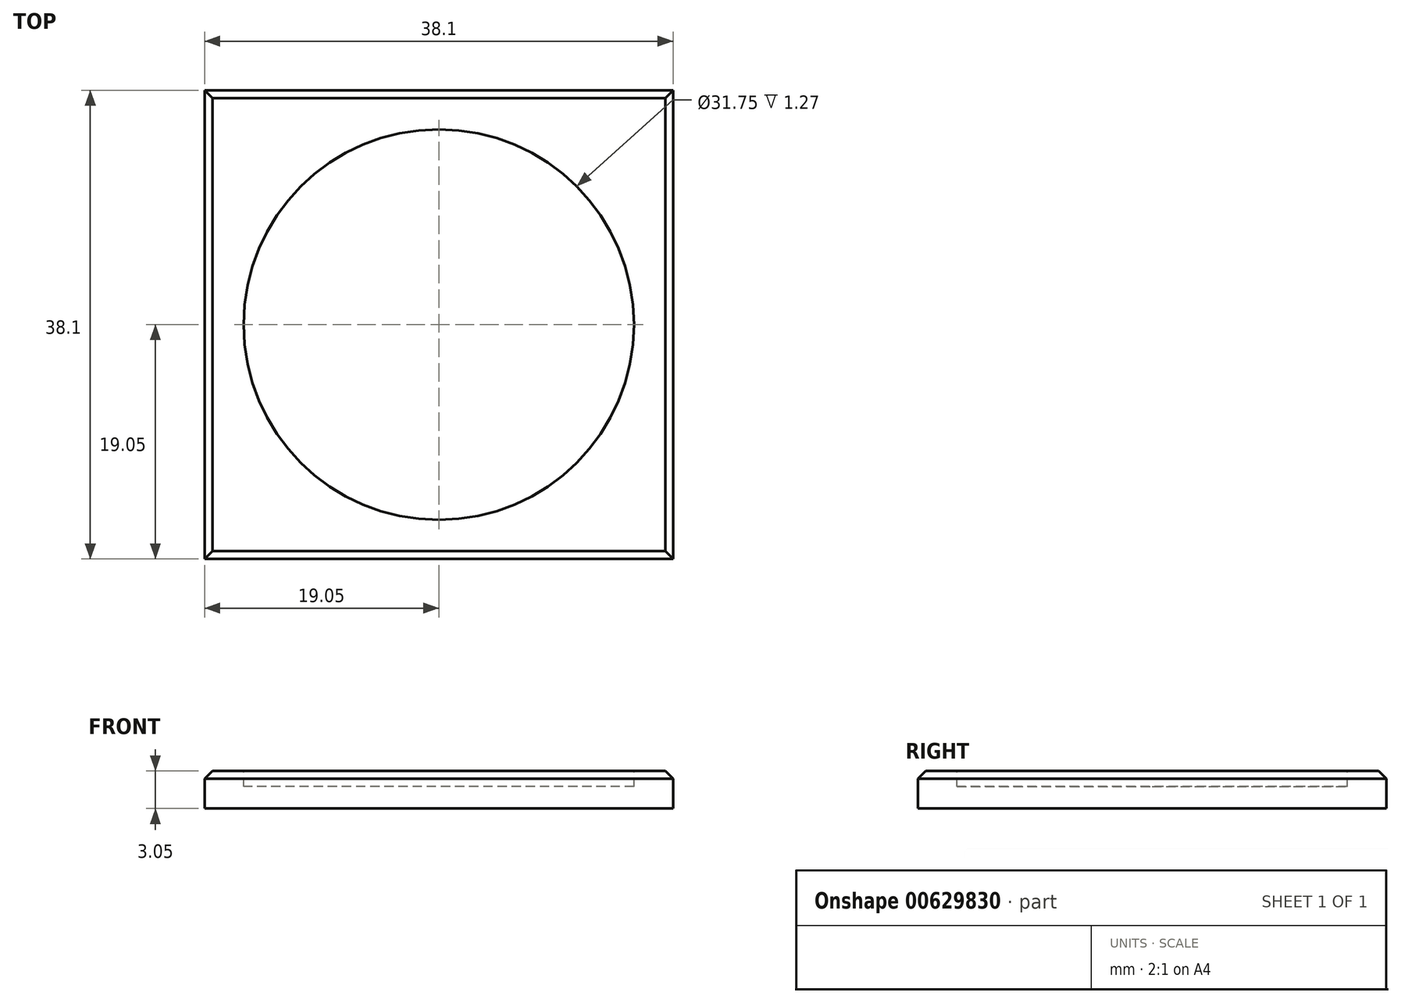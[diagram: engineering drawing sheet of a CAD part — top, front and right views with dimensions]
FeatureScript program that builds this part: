
annotation { "Feature Type Name" : "Feature", "Feature Type Description" : "" }
export const myFeature = defineFeature(function(context is Context, id is Id, definition is map)
    precondition{}
    {
        {
            var Q0;
            Q0=qCreatedBy(makeId("Top.planeOp"),FACE);
            var sketch = newSketch(context, id + "F0", { "sketchPlane" : qUnion([Q0])});
            skLineSegment(sketch, "E0.bottom", {"start": v(19.05, -19.05) * mm, "end": v(-19.05, -19.05) * mm});
            skLineSegment(sketch, "E0.top", {"start": v(19.05, 19.05) * mm, "end": v(-19.05, 19.05) * mm});
            skLineSegment(sketch, "E0.left", {"start": v(19.05, -19.05) * mm, "end": v(19.05, 19.05) * mm});
            skLineSegment(sketch, "E0.right", {"start": v(-19.05, -19.05) * mm, "end": v(-19.05, 19.05) * mm});
            skPoint(sketch, "E0.middle", {"position": v(0, 0) * mm});
            skSolve(sketch);
        }
        {
            var Q0;
            Q0=makeQuery(id+"F0.imprint","IMPRINT",FACE,{"disambiguationData":[TD([[makeQuery(id+"F0.imprint","IMPRINT",EDGE,{"derivedFrom":sQuery(id+"F0.wireOp",EDGE,"E0.bottom")}),-1.0]])]});
            extrude(context, id + "F1", {"entities" : qUnion([Q0]), "depth" : 3.05 * mm, "offsetDistance" : 25.4 * mm});
        }
        {
            var Q0;
            Q0=makeQuery(id+"F1.opExtrude","CAP_FACE",FACE,{"disambiguationData":[OSD([sQuery(id+"F0.wireOp",EDGE,"E0.bottom"),sQuery(id+"F0.wireOp",EDGE,"E0.top"),sQuery(id+"F0.wireOp",EDGE,"E0.left"),sQuery(id+"F0.wireOp",EDGE,"E0.right")])],"isStart":false});
            var sketch = newSketch(context, id + "F2", { "sketchPlane" : qUnion([Q0])});
            skCircle(sketch, "E1", {"center": v(0, 0) * mm, "radius": 15.88 * mm});
            skSolve(sketch);
        }
        {
            var Q0;
            Q0=makeQuery(id+"F2.imprint","IMPRINT",FACE,{"disambiguationData":[TD([[makeQuery(id+"F2.imprint","IMPRINT",EDGE,{"derivedFrom":sQuery(id+"F2.wireOp",EDGE,"E1")}),1.0]])]});
            extrude(context, id + "F3", {"entities" : qUnion([Q0]), "operationType" : NewBodyOperationType.REMOVE, "oppositeDirection" : true, "depth" : 1.27 * mm, "offsetDistance" : 25.4 * mm});
        }
        {
            var Q0;
            Q0=makeQuery(id+"F1.opExtrude","SWEPT_FACE",FACE,{"disambiguationData":[OSD([sQuery(id+"F0.wireOp",EDGE,"E0.bottom")])]});
            var sketch = newSketch(context, id + "F4", { "sketchPlane" : qUnion([Q0])});
            skLineSegment(sketch, "E2.bottom", {"start": v(-19.05, 3.05) * mm, "end": v(-18.41, 3.05) * mm});
            skLineSegment(sketch, "E2.left", {"start": v(-19.05, 3.05) * mm, "end": v(-19.05, 2.41) * mm});
            skLineSegment(sketch, "E3", {"start": v(-18.41, 3.05) * mm, "end": v(-19.05, 2.41) * mm});
            skLineSegment(sketch, "E4", {"start": v(18.41, 3.05) * mm, "end": v(19.05, 2.41) * mm});
            skLineSegment(sketch, "E5", {"start": v(19.05, 2.41) * mm, "end": v(19.05, 3.05) * mm});
            skLineSegment(sketch, "E6", {"start": v(19.05, 3.05) * mm, "end": v(18.41, 3.05) * mm});
            skSolve(sketch);
        }
        {
            var Q0;
            Q0=makeQuery(id+"F4.imprint","IMPRINT",FACE,{"disambiguationData":[TD([[makeQuery(id+"F4.imprint","IMPRINT",EDGE,{"derivedFrom":sQuery(id+"F4.wireOp",EDGE,"E2.bottom")}),1.0]])]});
            var Q1;
            Q1=makeQuery(id+"F4.imprint","IMPRINT",FACE,{"disambiguationData":[TD([[makeQuery(id+"F4.imprint","IMPRINT",EDGE,{"derivedFrom":sQuery(id+"F4.wireOp",EDGE,"E4")}),1.0]])]});
            extrude(context, id + "F5", {"entities" : qUnion([Q0, Q1]), "operationType" : NewBodyOperationType.REMOVE, "endBound" : BoundingType.THROUGH_ALL, "oppositeDirection" : true, "depth" : 25.4 * mm, "offsetDistance" : 25.4 * mm});
        }
        {
            var Q0;
            Q0=makeQuery(id+"F1.opExtrude","SWEPT_FACE",FACE,{"disambiguationData":[OSD([sQuery(id+"F0.wireOp",EDGE,"E0.right")])]});
            var sketch = newSketch(context, id + "F6", { "sketchPlane" : qUnion([Q0])});
            skLineSegment(sketch, "E7.bottom", {"start": v(-19.05, 3.05) * mm, "end": v(-18.41, 3.05) * mm});
            skLineSegment(sketch, "E7.left", {"start": v(-19.05, 3.05) * mm, "end": v(-19.05, 2.41) * mm});
            skLineSegment(sketch, "E8", {"start": v(-18.41, 3.05) * mm, "end": v(-19.05, 2.41) * mm});
            skLineSegment(sketch, "E9", {"start": v(18.42, 3.05) * mm, "end": v(19.05, 2.41) * mm});
            skLineSegment(sketch, "E10", {"start": v(19.05, 2.41) * mm, "end": v(19.05, 3.05) * mm});
            skLineSegment(sketch, "E11", {"start": v(19.05, 3.05) * mm, "end": v(18.42, 3.05) * mm});
            skSolve(sketch);
        }
        {
            var Q0;
            Q0=makeQuery(id+"F6.imprint","IMPRINT",FACE,{"disambiguationData":[TD([[makeQuery(id+"F6.imprint","IMPRINT",EDGE,{"derivedFrom":sQuery(id+"F6.wireOp",EDGE,"E7.bottom")}),-1.0]])]});
            var Q1;
            Q1=makeQuery(id+"F6.imprint","IMPRINT",FACE,{"disambiguationData":[TD([[makeQuery(id+"F6.imprint","IMPRINT",EDGE,{"derivedFrom":sQuery(id+"F6.wireOp",EDGE,"E9")}),1.0]])]});
            extrude(context, id + "F7", {"entities" : qUnion([Q0, Q1]), "operationType" : NewBodyOperationType.REMOVE, "endBound" : BoundingType.THROUGH_ALL, "oppositeDirection" : true, "depth" : 25.4 * mm, "offsetDistance" : 25.4 * mm});
        }
    });
